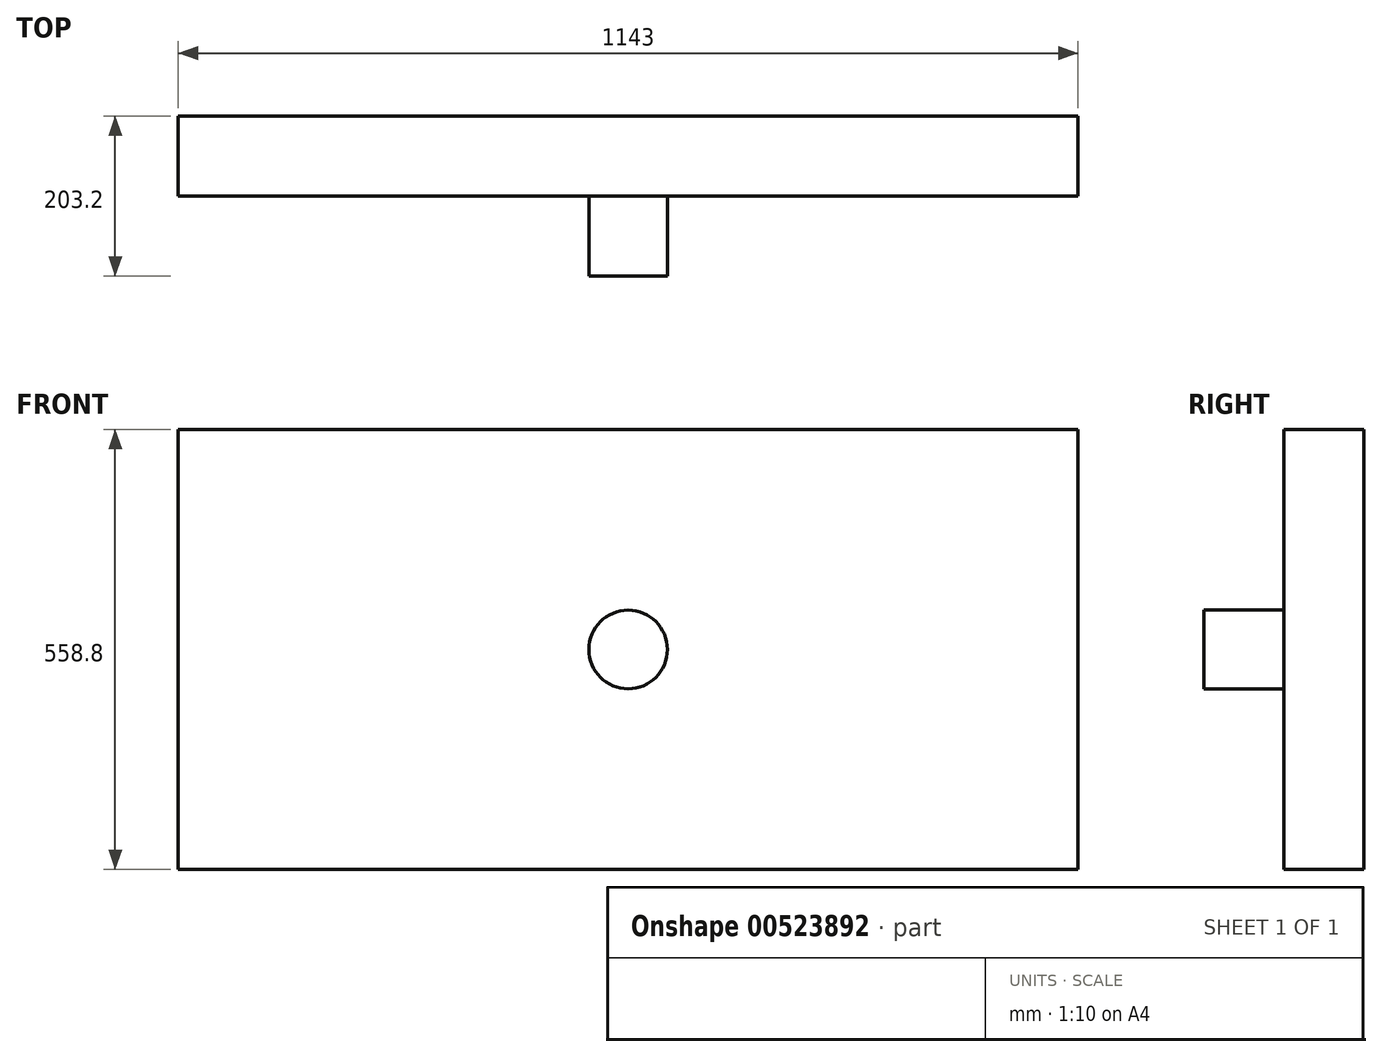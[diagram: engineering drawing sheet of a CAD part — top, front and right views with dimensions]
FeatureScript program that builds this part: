
annotation { "Feature Type Name" : "Feature", "Feature Type Description" : "" }
export const myFeature = defineFeature(function(context is Context, id is Id, definition is map)
    precondition{}
    {
        {
            var Q0;
            Q0=qCreatedBy(makeId("Front.planeOp"),FACE);
            var sketch = newSketch(context, id + "F0", { "sketchPlane" : qUnion([Q0])});
            skLineSegment(sketch, "E0.bottom", {"start": v(-571.5, 279.4) * mm, "end": v(571.5, 279.4) * mm});
            skLineSegment(sketch, "E0.top", {"start": v(-571.5, -279.4) * mm, "end": v(571.5, -279.4) * mm});
            skLineSegment(sketch, "E0.left", {"start": v(-571.5, 279.4) * mm, "end": v(-571.5, -279.4) * mm});
            skLineSegment(sketch, "E0.right", {"start": v(571.5, 279.4) * mm, "end": v(571.5, -279.4) * mm});
            skPoint(sketch, "E0.middle", {"position": v(0, 0) * mm});
            skSolve(sketch);
        }
        {
            var Q0;
            Q0 = qSketchRegion(id + "F0", true);
            extrude(context, id + "F1", {"entities" : qUnion([Q0]), "depth" : 101.6 * mm, "offsetDistance" : 25.4 * mm});
        }
        {
            var Q0;
            Q0=makeQuery(id+"F1.opExtrude","CAP_FACE",FACE,{"disambiguationData":[OSD([sQuery(id+"F0.wireOp",EDGE,"E0.bottom"),sQuery(id+"F0.wireOp",EDGE,"E0.top"),sQuery(id+"F0.wireOp",EDGE,"E0.left"),sQuery(id+"F0.wireOp",EDGE,"E0.right")])],"isStart":false});
            var sketch = newSketch(context, id + "F2", { "sketchPlane" : qUnion([Q0])});
            skCircle(sketch, "E1", {"center": v(0, 0) * mm, "radius": 49.96 * mm});
            skLineSegment(sketch, "E2", {"start": v(0, 279.4) * mm, "end": v(0, -279.4) * mm});
            skLineSegment(sketch, "E3", {"start": v(-571.5, 0) * mm, "end": v(571.5, 0) * mm});
            skSolve(sketch);
        }
        {
            var Q0;
            Q0 = qSketchRegion(id + "F2", true);
            extrude(context, id + "F3", {"entities" : qUnion([Q0]), "operationType" : NewBodyOperationType.ADD, "depth" : 101.6 * mm, "offsetDistance" : 25.4 * mm});
        }
    });
